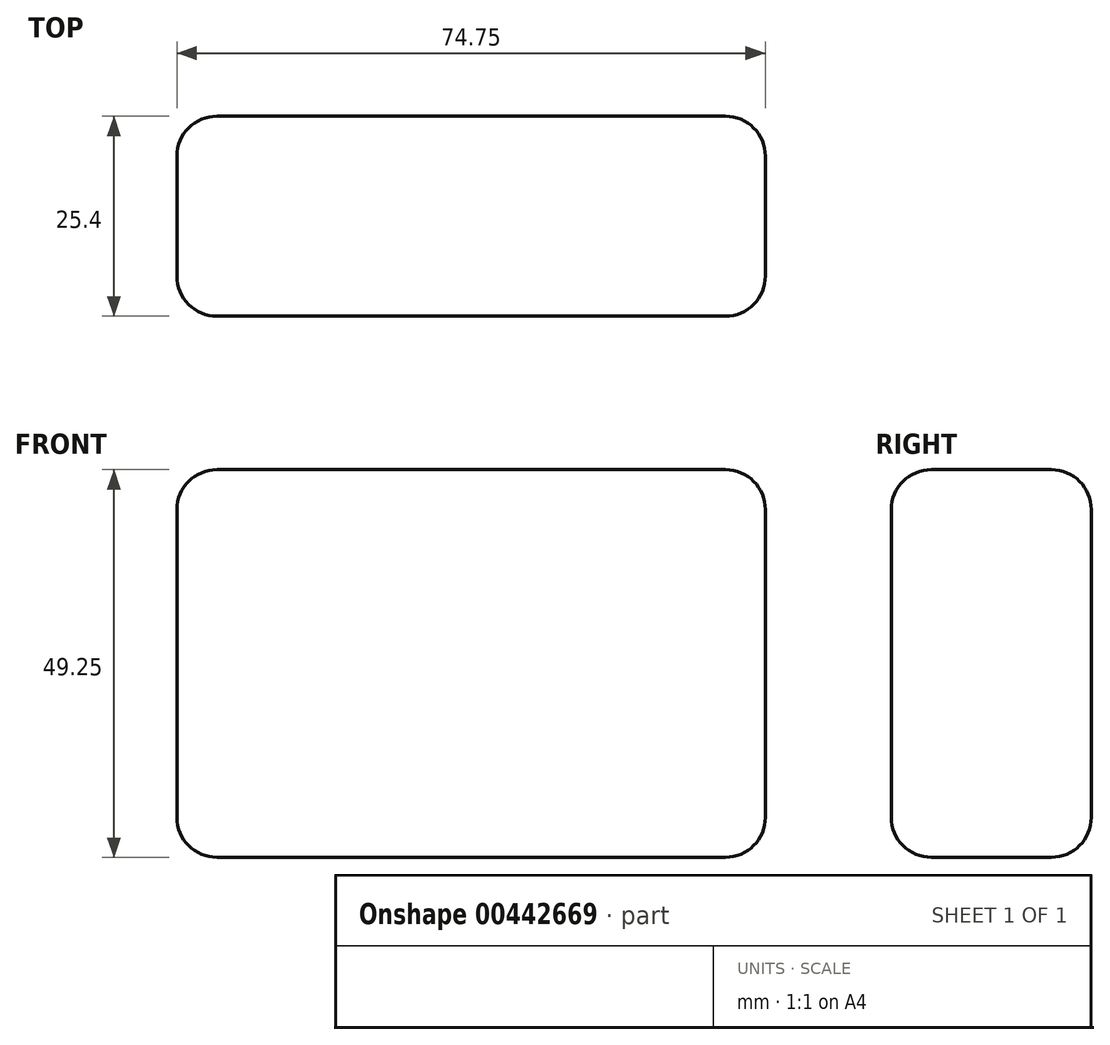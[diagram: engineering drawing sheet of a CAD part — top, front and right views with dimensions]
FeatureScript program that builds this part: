
annotation { "Feature Type Name" : "Feature", "Feature Type Description" : "" }
export const myFeature = defineFeature(function(context is Context, id is Id, definition is map)
    precondition{}
    {
        {
            var Q0;
            Q0=qCreatedBy(makeId("Front.planeOp"),FACE);
            var sketch = newSketch(context, id + "F0", { "sketchPlane" : qUnion([Q0])});
            skLineSegment(sketch, "E0.bottom", {"start": v(0, 0) * mm, "end": v(74.75, 0) * mm});
            skLineSegment(sketch, "E0.top", {"start": v(0, 49.25) * mm, "end": v(74.75, 49.25) * mm});
            skLineSegment(sketch, "E0.left", {"start": v(0, 0) * mm, "end": v(0, 49.25) * mm});
            skLineSegment(sketch, "E0.right", {"start": v(74.75, 0) * mm, "end": v(74.75, 49.25) * mm});
            skSolve(sketch);
        }
        {
            var Q0;
            Q0=makeQuery(id+"F0.imprint","IMPRINT",FACE,{"disambiguationData":[TD([[makeQuery(id+"F0.imprint","IMPRINT",EDGE,{"derivedFrom":sQuery(id+"F0.wireOp",EDGE,"E0.bottom")}),1.0]])]});
            extrude(context, id + "F1", {"entities" : qUnion([Q0]), "depth" : 25.4 * mm});
        }
        {
            var Q0;
            Q0=makeQuery(id+"F1.opExtrude","CAP_EDGE",EDGE,{"disambiguationData":[OSD([sQuery(id+"F0.wireOp",EDGE,"E0.top")])],"isStart":false});
            var Q1;
            Q1=makeQuery(id+"F1.opExtrude","SWEPT_EDGE",EDGE,{"disambiguationData":[OSD([sQuery(id+"F0.wireOp",EDGE,"E0.top"),sQuery(id+"F0.wireOp",EDGE,"E0.right")])]});
            var Q2;
            Q2=makeQuery(id+"F1.opExtrude","CAP_EDGE",EDGE,{"disambiguationData":[OSD([sQuery(id+"F0.wireOp",EDGE,"E0.top")])],"isStart":true});
            var Q3;
            Q3=makeQuery(id+"F1.opExtrude","SWEPT_EDGE",EDGE,{"disambiguationData":[OSD([sQuery(id+"F0.wireOp",EDGE,"E0.top"),sQuery(id+"F0.wireOp",EDGE,"E0.left")])]});
            var Q4;
            Q4=makeQuery(id+"F1.opExtrude","CAP_EDGE",EDGE,{"disambiguationData":[OSD([sQuery(id+"F0.wireOp",EDGE,"E0.right")])],"isStart":false});
            var Q5;
            Q5=makeQuery(id+"F1.opExtrude","CAP_EDGE",EDGE,{"disambiguationData":[OSD([sQuery(id+"F0.wireOp",EDGE,"E0.right")])],"isStart":true});
            var Q6;
            Q6=makeQuery(id+"F1.opExtrude","CAP_EDGE",EDGE,{"disambiguationData":[OSD([sQuery(id+"F0.wireOp",EDGE,"E0.left")])],"isStart":true});
            var Q7;
            Q7=makeQuery(id+"F1.opExtrude","CAP_EDGE",EDGE,{"disambiguationData":[OSD([sQuery(id+"F0.wireOp",EDGE,"E0.left")])],"isStart":false});
            var Q8;
            Q8=makeQuery(id+"F1.opExtrude","SWEPT_EDGE",EDGE,{"disambiguationData":[OSD([sQuery(id+"F0.wireOp",EDGE,"E0.bottom"),sQuery(id+"F0.wireOp",EDGE,"E0.left")])]});
            var Q9;
            Q9=makeQuery(id+"F1.opExtrude","CAP_EDGE",EDGE,{"disambiguationData":[OSD([sQuery(id+"F0.wireOp",EDGE,"E0.bottom")])],"isStart":true});
            var Q10;
            Q10=makeQuery(id+"F1.opExtrude","SWEPT_FACE",FACE,{"disambiguationData":[OSD([sQuery(id+"F0.wireOp",EDGE,"E0.bottom")])]});
            var Q11;
            Q11=makeQuery(id+"F1.opExtrude","SWEPT_EDGE",EDGE,{"disambiguationData":[OSD([sQuery(id+"F0.wireOp",EDGE,"E0.bottom"),sQuery(id+"F0.wireOp",EDGE,"E0.right")])]});
            var Q12;
            Q12=makeQuery(id+"F1.opExtrude","CAP_EDGE",EDGE,{"disambiguationData":[OSD([sQuery(id+"F0.wireOp",EDGE,"E0.bottom")])],"isStart":false});
            fillet(context, id + "F2", {"entities" : qUnion([Q0, Q1, Q2, Q3, Q4, Q5, Q6, Q7, Q8, Q9, Q10, Q11, Q12]), "radius" : 5.08 * mm, "tangentPropagation" : true, "allowEdgeOverflow" : false});
        }
    });
